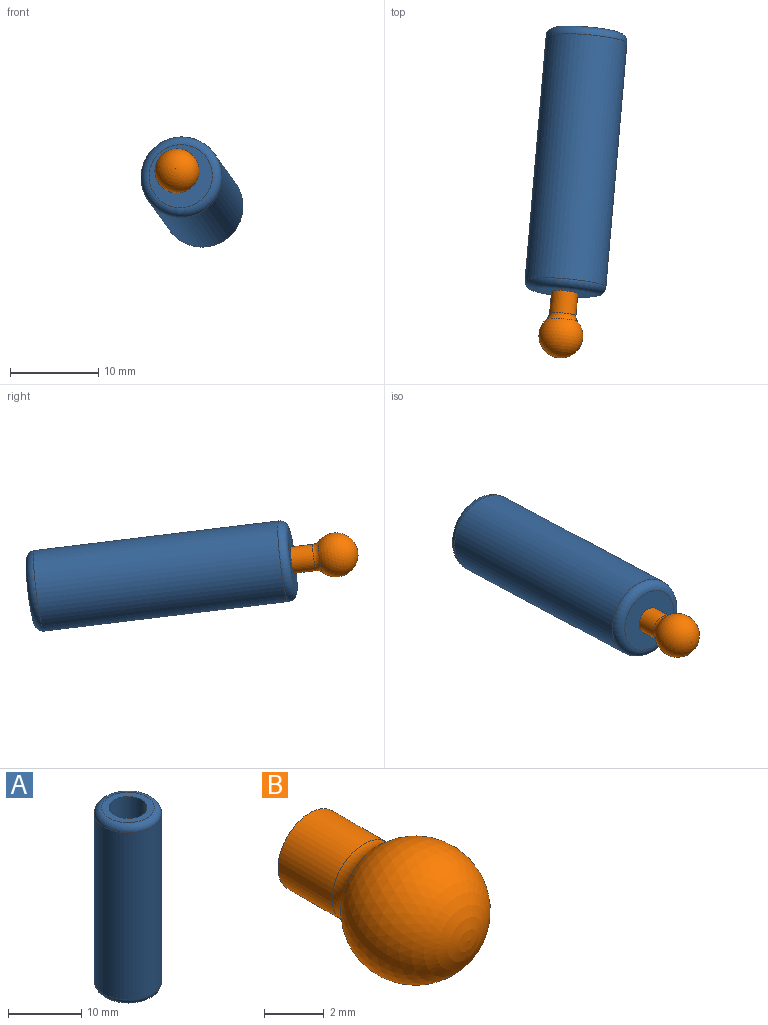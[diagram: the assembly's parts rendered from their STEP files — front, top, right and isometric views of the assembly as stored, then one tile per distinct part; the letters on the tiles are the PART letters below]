
ASSEMBLY  parts=2 mates=1
PART A: 7 faces, bbox 10x10x30 mm
  f0: cylinder r=2.6mm len=28mm, axis (0,0,-1), area 457.4mm2, adj f2,f4
  f1: cylinder r=4.6mm len=28mm, axis (0,0,-1), area 809.3mm2, adj f5,f6
  f2: plane 7.2x7.2mm, normal (0,0,1), area 19.5mm2, adj f0,f6
  f3: plane 7.2x7.2mm, normal (0,0,-1), area 40.7mm2, adj f5
  f4: plane 5.2x5.2mm, normal (0,0,1), area 21.2mm2, adj f0
  f5: torus R=3.6mm, axis (0,0,1), area 41.8mm2, adj f1,f3
  f6: torus R=3.6mm, axis (0,0,1), area 41.8mm2, adj f1,f2
PART B: 4 faces, bbox 5x7.5x5 mm
  f0: sphere r=2.5mm, area 66.8mm2, adj f3
  f1: cylinder r=1.5mm len=3mm, axis (0,-1,0), area 24mm2, adj f2,f3
  f2: plane 3x3mm, normal (0,1,0), area 7.1mm2, adj f1
  f3: torus R=2.5mm, axis (0,-1,0), area 7.8mm2, adj f0,f1
PLACE A rot(axis=(-0.8,0.48,0.36),106.6deg) t=(0,0,0)mm fixed
PLACE B rot(axis=(-0.24,-0.97,-0.08),34.3deg) t=(-0.43,-4.95,0.6)mm
MATE fastened B.f1 <-> A.f1  axis (0.09,0.99,-0.12) through (0,0,0)mm
